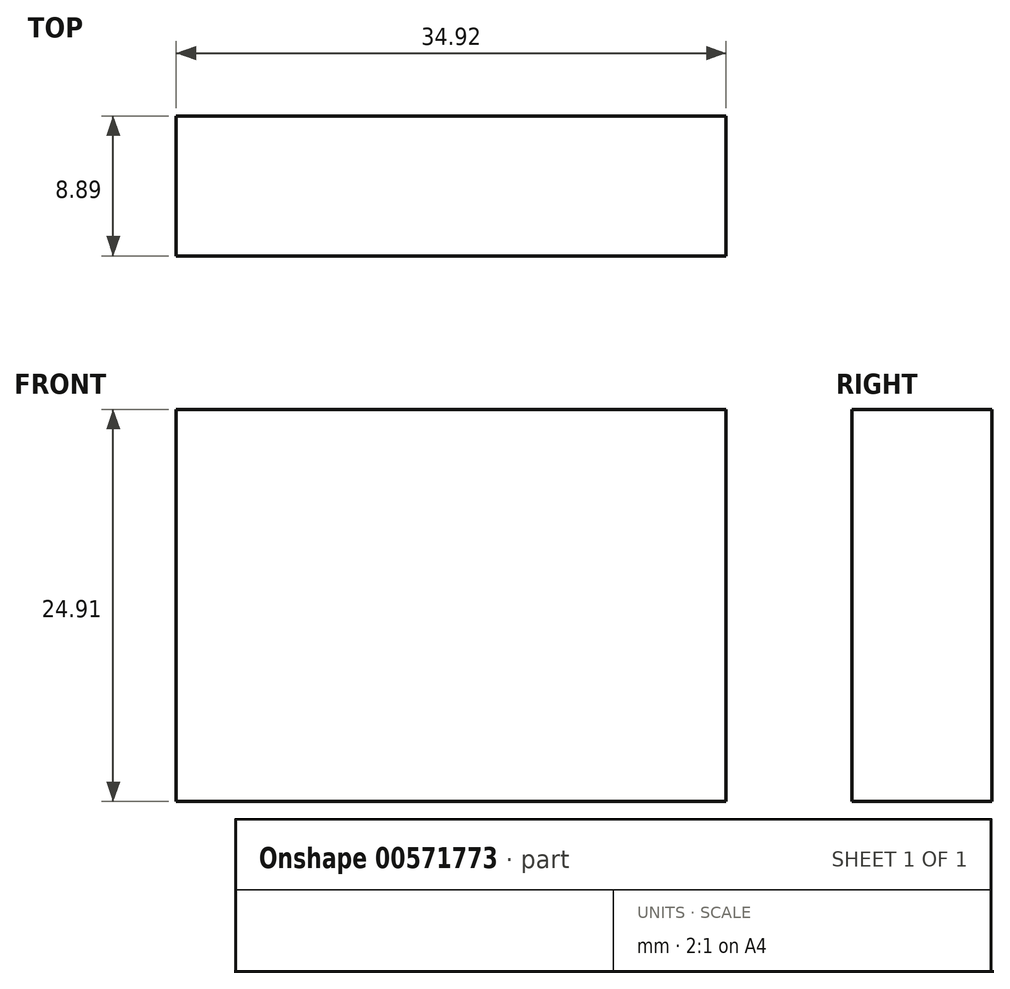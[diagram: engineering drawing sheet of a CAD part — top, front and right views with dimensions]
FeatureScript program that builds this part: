
annotation { "Feature Type Name" : "Feature", "Feature Type Description" : "" }
export const myFeature = defineFeature(function(context is Context, id is Id, definition is map)
    precondition{}
    {
        {
            var Q0;
            Q0=qCreatedBy(makeId("Front.planeOp"),FACE);
            var sketch = newSketch(context, id + "F0", { "sketchPlane" : qUnion([Q0])});
            skPoint(sketch, "E0.0", {"position": v(0, 0) * mm});
            skLineSegment(sketch, "E1.bottom", {"start": v(0, 0) * mm, "end": v(34.92, 0) * mm});
            skLineSegment(sketch, "E1.top", {"start": v(0, 24.9) * mm, "end": v(34.93, 24.9) * mm});
            skLineSegment(sketch, "E1.left", {"start": v(0, 0) * mm, "end": v(0, 24.9) * mm});
            skLineSegment(sketch, "E1.right", {"start": v(34.93, 0) * mm, "end": v(34.93, 24.9) * mm});
            skSolve(sketch);
        }
        {
            var Q0;
            Q0 = qSketchRegion(id + "F0", true);
            extrude(context, id + "F1", {"entities" : qUnion([Q0]), "depth" : 8.9 * mm, "offsetDistance" : 25.4 * mm});
        }
    });
